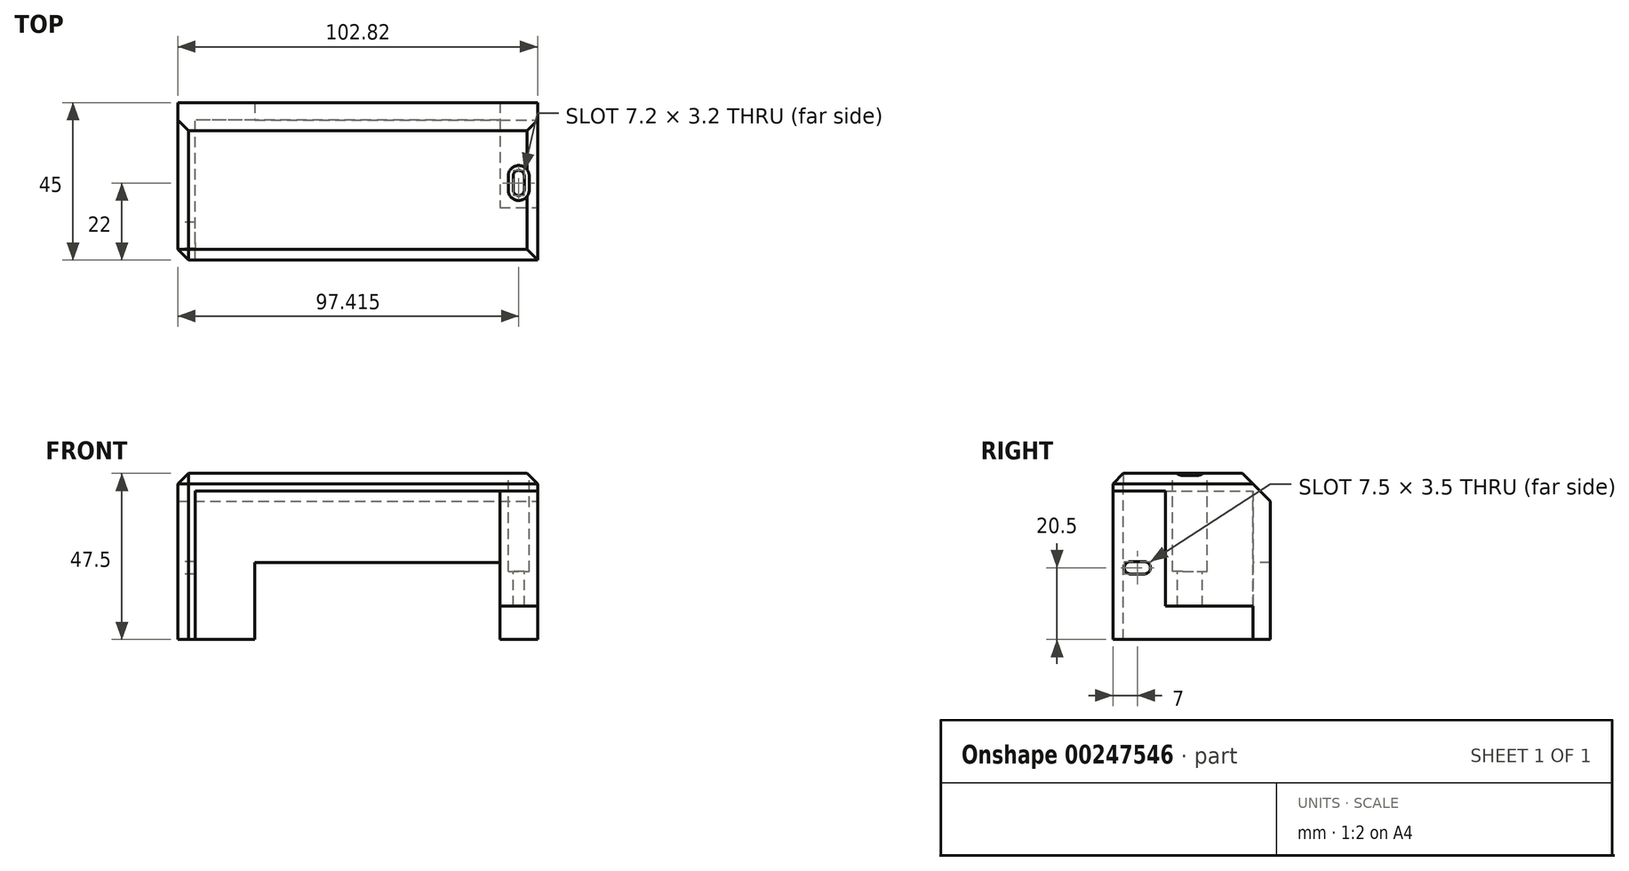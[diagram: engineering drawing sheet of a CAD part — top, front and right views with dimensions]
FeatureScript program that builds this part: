
annotation { "Feature Type Name" : "Feature", "Feature Type Description" : "" }
export const myFeature = defineFeature(function(context is Context, id is Id, definition is map)
    precondition{}
    {
        {
            var Q0;
            Q0=qCreatedBy(makeId("Front.planeOp"),FACE);
            var sketch = newSketch(context, id + "F0", { "sketchPlane" : qUnion([Q0])});
            skLineSegment(sketch, "E0.left", {"start": v(48.9, -21.25) * mm, "end": v(48.9, 21.25) * mm});
            skLineSegment(sketch, "E0.right", {"start": v(-48.9, -21.25) * mm, "end": v(-48.9, 21.25) * mm});
            skPoint(sketch, "E0.middle", {"position": v(0, 0) * mm});
            skLineSegment(sketch, "E1.bottom", {"start": v(-53.9, 26.25) * mm, "end": v(48.9, 26.25) * mm});
            skLineSegment(sketch, "E1.left", {"start": v(-53.9, 26.25) * mm, "end": v(-53.9, -21.25) * mm});
            skLineSegment(sketch, "E2", {"start": v(38.14, 21.25) * mm, "end": v(38.13, -21.25) * mm});
            skLineSegment(sketch, "E3", {"start": v(48.9, 26.25) * mm, "end": v(48.9, 21.25) * mm});
            skLineSegment(sketch, "E4", {"start": v(38.13, -11.75) * mm, "end": v(48.9, -11.75) * mm});
            skLineSegment(sketch, "E5", {"start": v(48.9, 21.25) * mm, "end": v(-48.9, 21.25) * mm});
            skLineSegment(sketch, "E6", {"start": v(48.9, -21.25) * mm, "end": v(-53.9, -21.25) * mm});
            skSolve(sketch);
        }
        {
            var Q0;
            {var subQ3=sQuery(id+"F0.wireOp",EDGE,"E0.right");Q0=makeQuery(id+"F0.imprint","IMPRINT",FACE,{"disambiguationData":[TD([[makeQuery(id+"F0.imprint","IMPRINT",EDGE,{"derivedFrom":subQ3}),1.0]])]});}
            extrude(context, id + "F1", {"entities" : qUnion([Q0]), "depth" : 15 * mm});
        }
        {
            var Q0;
            Q0 = qSketchRegion(id + "F0", true);
            extrude(context, id + "F2", {"entities" : qUnion([Q0]), "operationType" : NewBodyOperationType.ADD, "oppositeDirection" : true, "depth" : 30 * mm});
        }
        {
            var Q0;
            {var subQ1=sQuery(id+"F0.wireOp",EDGE,"E0.right");Q0=makeQuery(id+"F0.imprint","IMPRINT",FACE,{"disambiguationData":[TD([[makeQuery(id+"F0.imprint","IMPRINT",EDGE,{"derivedFrom":subQ1}),-1.0]])]});}
            var Q1;
            {var subQ3=sQuery(id+"F0.wireOp",EDGE,"E4");Q1=makeQuery(id+"F0.imprint","IMPRINT",FACE,{"disambiguationData":[TD([[makeQuery(id+"F0.imprint","IMPRINT",EDGE,{"derivedFrom":subQ3}),-1.0]])]});}
            extrude(context, id + "F3", {"entities" : qUnion([Q0, Q1]), "operationType" : NewBodyOperationType.REMOVE, "oppositeDirection" : true, "depth" : 25 * mm});
        }
        {
            var Q0;
            {var subQ0=sQuery(id+"F0.wireOp",EDGE,"E1.bottom");Q0=makeQuery(id+"F2.boolean.opBoolean","MERGE",FACE,{"derivedFrom":[makeQuery(id+"F1.opExtrude","SWEPT_FACE",FACE,{"disambiguationData":[OSD([subQ0])]}),makeQuery(id+"F2.opExtrude","SWEPT_FACE",FACE,{"disambiguationData":[OSD([subQ0])]})]});}
            var sketch = newSketch(context, id + "F4", { "sketchPlane" : qUnion([Q0])});
            skCircle(sketch, "E7", {"center": v(43.5, 5) * mm, "radius": 1.6 * mm});
            skCircle(sketch, "E8", {"center": v(43.5, 5) * mm, "radius": 3 * mm});
            skCircle(sketch, "E9", {"center": v(43.5, 9) * mm, "radius": 1.6 * mm});
            skCircle(sketch, "E10", {"center": v(43.5, 9) * mm, "radius": 3 * mm});
            skLineSegment(sketch, "E11", {"start": v(40.5, 5) * mm, "end": v(40.5, 9) * mm});
            skLineSegment(sketch, "E12", {"start": v(46.5, 5) * mm, "end": v(46.5, 9) * mm});
            skLineSegment(sketch, "E13", {"start": v(41.9, 5) * mm, "end": v(41.9, 9) * mm});
            skLineSegment(sketch, "E14", {"start": v(45.1, 9) * mm, "end": v(45.1, 5) * mm});
            skSolve(sketch);
        }
        {
            var Q0;
            {var subQ6=sQuery(id+"F4.wireOp",EDGE,"E13");var subQ7=sQuery(id+"F4.wireOp",EDGE,"E7");var subQ8=makeQuery(id+"F4.imprint","INTERSECT",VERTEX,{"derivedFrom":[subQ7,subQ6]});Q0=makeQuery(id+"F4.imprint","IMPRINT",FACE,{"disambiguationData":[TD([[makeQuery(id+"F4.imprint","IMPRINT",EDGE,{"disambiguationData":[TD([[subQ8,-1.0]])],"derivedFrom":subQ7}),-1.0]])]});}
            var Q1;
            {var subQ5=sQuery(id+"F4.wireOp",EDGE,"E8");var subQ7=sQuery(id+"F4.wireOp",EDGE,"E10");var subQ10=makeQuery(id+"F4.imprint","INTERSECT",VERTEX,{"disambiguationData":[OD(0.0)],"derivedFrom":[subQ5,subQ7]});Q1=makeQuery(id+"F4.imprint","IMPRINT",FACE,{"disambiguationData":[TD([[makeQuery(id+"F4.imprint","IMPRINT",EDGE,{"disambiguationData":[TD([[subQ10,-1.0]])],"derivedFrom":subQ5}),-1.0]])]});}
            var Q2;
            {var subQ0=sQuery(id+"F4.wireOp",EDGE,"E13");var subQ1=sQuery(id+"F4.wireOp",EDGE,"E8");var subQ2=makeQuery(id+"F4.imprint","INTERSECT",VERTEX,{"derivedFrom":[subQ1,subQ0]});Q2=makeQuery(id+"F4.imprint","IMPRINT",FACE,{"disambiguationData":[TD([[makeQuery(id+"F4.imprint","IMPRINT",EDGE,{"disambiguationData":[TD([[subQ2,-1.0]])],"derivedFrom":subQ1}),1.0]])]});}
            var Q3;
            {var subQ0=sQuery(id+"F4.wireOp",EDGE,"E10");var subQ1=sQuery(id+"F4.wireOp",EDGE,"E8");var subQ2=makeQuery(id+"F4.imprint","INTERSECT",VERTEX,{"disambiguationData":[OD(0.0)],"derivedFrom":[subQ1,subQ0]});Q3=makeQuery(id+"F4.imprint","IMPRINT",FACE,{"disambiguationData":[TD([[makeQuery(id+"F4.imprint","IMPRINT",EDGE,{"disambiguationData":[TD([[subQ2,-1.0]])],"derivedFrom":subQ1}),1.0]])]});}
            var Q4;
            {var subQ0=sQuery(id+"F4.wireOp",EDGE,"E12");Q4=makeQuery(id+"F4.imprint","IMPRINT",FACE,{"disambiguationData":[TD([[makeQuery(id+"F4.imprint","IMPRINT",EDGE,{"derivedFrom":subQ0}),1.0]])]});}
            var Q5;
            {var subQ0=sQuery(id+"F4.wireOp",EDGE,"E11");Q5=makeQuery(id+"F4.imprint","IMPRINT",FACE,{"disambiguationData":[TD([[makeQuery(id+"F4.imprint","IMPRINT",EDGE,{"derivedFrom":subQ0}),-1.0]])]});}
            extrude(context, id + "F5", {"entities" : qUnion([Q0, Q1, Q2, Q3, Q4, Q5]), "operationType" : NewBodyOperationType.REMOVE, "oppositeDirection" : true, "depth" : 28 * mm});
        }
        {
            var Q0;
            {var subQ0=sQuery(id+"F0.wireOp",EDGE,"E1.bottom");Q0=makeQuery(id+"F5.boolean.opBoolean","SPLIT",FACE,{"disambiguationData":[TD([makeQuery(id+"F5.opExtrude","SWEPT_FACE",FACE,{"disambiguationData":[OSD([sQuery(id+"F4.wireOp",EDGE,"E7")])]})])],"derivedFrom":makeQuery(id+"F2.boolean.opBoolean","MERGE",FACE,{"derivedFrom":[makeQuery(id+"F1.opExtrude","SWEPT_FACE",FACE,{"disambiguationData":[OSD([subQ0])]}),makeQuery(id+"F2.opExtrude","SWEPT_FACE",FACE,{"disambiguationData":[OSD([subQ0])]})]})});}
            extrude(context, id + "F6", {"entities" : qUnion([Q0]), "operationType" : NewBodyOperationType.REMOVE, "endBound" : BoundingType.THROUGH_ALL, "oppositeDirection" : true, "depth" : 25 * mm});
        }
        {
            var Q0;
            {var subQ0=sQuery(id+"F0.wireOp",EDGE,"E1.left");Q0=makeQuery(id+"F2.boolean.opBoolean","MERGE",FACE,{"derivedFrom":[makeQuery(id+"F1.opExtrude","SWEPT_FACE",FACE,{"disambiguationData":[OSD([subQ0])]}),makeQuery(id+"F2.opExtrude","SWEPT_FACE",FACE,{"disambiguationData":[OSD([subQ0])]})]});}
            var sketch = newSketch(context, id + "F7", { "sketchPlane" : qUnion([Q0])});
            skCircle(sketch, "E15", {"center": v(6, -0.75) * mm, "radius": 1.75 * mm});
            skCircle(sketch, "E16", {"center": v(10, -0.75) * mm, "radius": 1.75 * mm});
            skLineSegment(sketch, "E17", {"start": v(10, 1) * mm, "end": v(6, 1) * mm});
            skLineSegment(sketch, "E18", {"start": v(10, -2.5) * mm, "end": v(6, -2.5) * mm});
            skSolve(sketch);
        }
        {
            var Q0;
            Q0 = qSketchRegion(id + "F7", true);
            extrude(context, id + "F8", {"entities" : qUnion([Q0]), "operationType" : NewBodyOperationType.REMOVE, "oppositeDirection" : true, "depth" : 6 * mm});
        }
        {
            var Q0;
            {var subQ0=sQuery(id+"F0.wireOp",EDGE,"E1.left");var subQ1=sQuery(id+"F0.wireOp",EDGE,"E1.bottom");Q0=makeQuery(id+"F2.boolean.opBoolean","MERGE",EDGE,{"derivedFrom":[makeQuery(id+"F1.opExtrude","SWEPT_EDGE",EDGE,{"disambiguationData":[OSD([subQ1,subQ0])]}),makeQuery(id+"F2.opExtrude","SWEPT_EDGE",EDGE,{"disambiguationData":[OSD([subQ1,subQ0])]})]});}
            var Q1;
            Q1=makeQuery(id+"F1.opExtrude","CAP_EDGE",EDGE,{"disambiguationData":[OSD([sQuery(id+"F0.wireOp",EDGE,"E1.bottom")])],"isStart":false});
            var Q2;
            Q2=makeQuery(id+"F1.opExtrude","CAP_EDGE",EDGE,{"disambiguationData":[OSD([sQuery(id+"F0.wireOp",EDGE,"E1.left")])],"isStart":false});
            var Q3;
            {var subQ0=sQuery(id+"F0.wireOp",EDGE,"E3");var subQ1=sQuery(id+"F0.wireOp",EDGE,"E1.bottom");Q3=makeQuery(id+"F2.boolean.opBoolean","MERGE",EDGE,{"derivedFrom":[makeQuery(id+"F1.opExtrude","SWEPT_EDGE",EDGE,{"disambiguationData":[OSD([subQ1,subQ0])]}),makeQuery(id+"F2.opExtrude","SWEPT_EDGE",EDGE,{"disambiguationData":[OSD([subQ1,subQ0])]})]});}
            chamfer(context, id + "F9", {"entities" : qUnion([Q0, Q1, Q2, Q3]), "width" : 3 * mm, "tangentPropagation" : true});
        }
        {
            var Q0;
            Q0=makeQuery(id+"F2.opExtrude","CAP_EDGE",EDGE,{"disambiguationData":[OSD([sQuery(id+"F0.wireOp",EDGE,"E1.bottom")])],"isStart":false});
            chamfer(context, id + "F10", {"entities" : qUnion([Q0]), "width" : 8 * mm, "tangentPropagation" : true});
        }
        {
            var Q0;
            Q0=makeQuery(id+"F3.boolean.opBoolean","COPY",FACE,{"derivedFrom":makeQuery(id+"F3.opExtrude","CAP_FACE",FACE,{"disambiguationData":[OSD([sQuery(id+"F0.wireOp",EDGE,"E0.left"),sQuery(id+"F0.wireOp",EDGE,"E0.right"),sQuery(id+"F0.wireOp",EDGE,"E2"),sQuery(id+"F0.wireOp",EDGE,"E4"),sQuery(id+"F0.wireOp",EDGE,"E5"),sQuery(id+"F0.wireOp",EDGE,"E6")])],"isStart":false})});
            var sketch = newSketch(context, id + "F11", { "sketchPlane" : qUnion([Q0])});
            skLineSegment(sketch, "E19.bottom", {"start": v(-31.9, 0.75) * mm, "end": v(38.14, 0.75) * mm});
            skLineSegment(sketch, "E19.top", {"start": v(-31.9, -21.25) * mm, "end": v(38.14, -21.25) * mm});
            skLineSegment(sketch, "E19.left", {"start": v(-31.9, 0.75) * mm, "end": v(-31.9, -21.25) * mm});
            skLineSegment(sketch, "E19.right", {"start": v(38.14, 0.75) * mm, "end": v(38.14, -21.25) * mm});
            skSolve(sketch);
        }
        {
            var Q0;
            Q0 = qSketchRegion(id + "F11", true);
            extrude(context, id + "F12", {"entities" : qUnion([Q0]), "operationType" : NewBodyOperationType.REMOVE, "oppositeDirection" : true, "depth" : 25 * mm});
        }
    });
